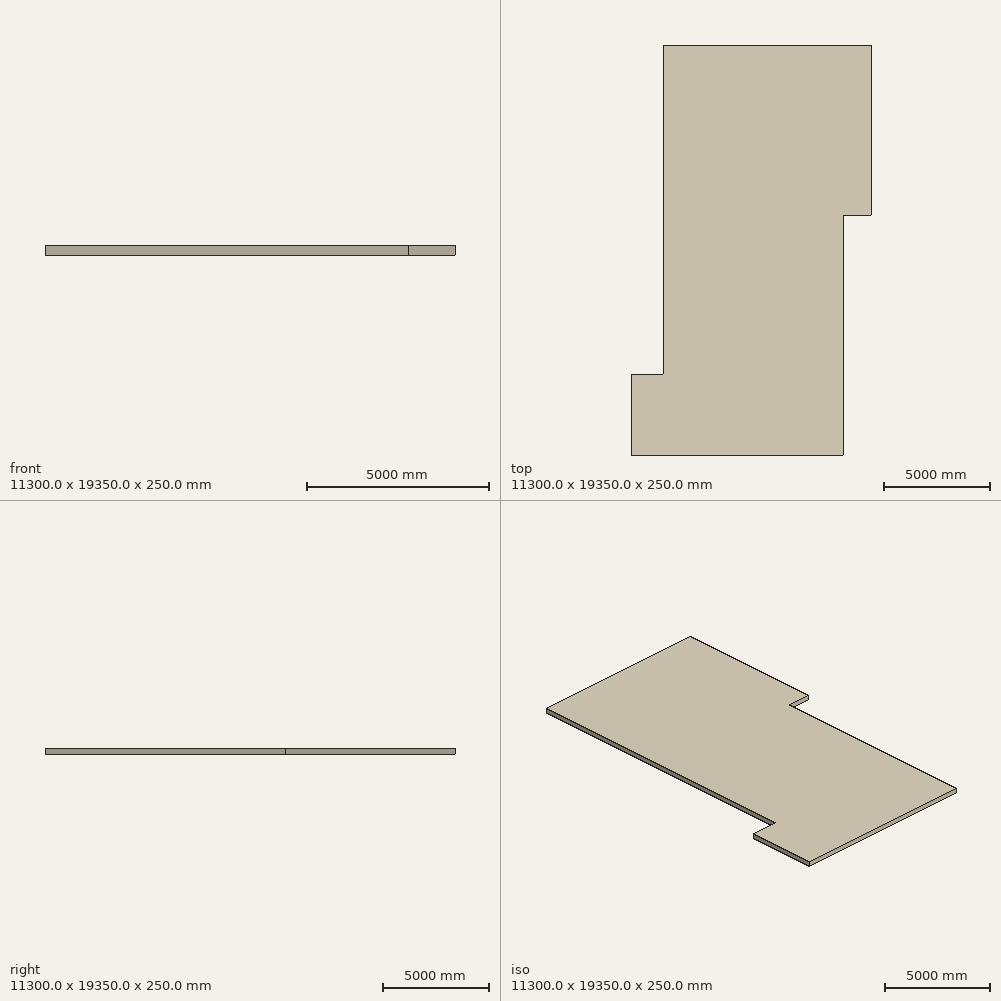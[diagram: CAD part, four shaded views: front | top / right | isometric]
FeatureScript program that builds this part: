
annotation { "Feature Type Name" : "Feature", "Feature Type Description" : "" }
export const myFeature = defineFeature(function(context is Context, id is Id, definition is map)
    precondition{}
    {
        {
            var Q0;
            Q0=qCreatedBy(makeId("Top.planeOp"),FACE);
            var sketch = newSketch(context, id + "F0", { "sketchPlane" : qUnion([Q0])});
            skLineSegment(sketch, "E0.bottom", {"start": v(-8628.68, 11353.51) * mm, "end": v(621.32, 11353.51) * mm});
            skLineSegment(sketch, "E0.top", {"start": v(-6878.68, 3353.51) * mm, "end": v(621.32, 3353.51) * mm});
            skLineSegment(sketch, "E0.right", {"start": v(621.32, 11353.51) * mm, "end": v(621.32, 3353.51) * mm});
            skLineSegment(sketch, "E1", {"start": v(-6878.68, 3353.51) * mm, "end": v(-8628.68, 11353.51) * mm});
            skSolve(sketch);
        }
        {
            var Q0;
            Q0 = qSketchRegion(id + "F0", true);
            extrude(context, id + "F1", {"entities" : qUnion([Q0]), "oppositeDirection" : true, "depth" : 250 * mm});
        }
        {
            var Q0;
            Q0=makeQuery(id+"F1.opExtrude","CAP_FACE",FACE,{"disambiguationData":[OSD([sQuery(id+"F0.wireOp",EDGE,"E0.bottom"),sQuery(id+"F0.wireOp",EDGE,"E0.top"),sQuery(id+"F0.wireOp",EDGE,"E0.right"),sQuery(id+"F0.wireOp",EDGE,"E1")])],"isStart":true});
            var sketch = newSketch(context, id + "F2", { "sketchPlane" : qUnion([Q0])});
            skLineSegment(sketch, "E2.bottom", {"start": v(-678.68, 3353.51) * mm, "end": v(-10678.68, 3353.51) * mm});
            skLineSegment(sketch, "E2.top", {"start": v(-678.68, -7996.49) * mm, "end": v(-10678.68, -7996.49) * mm});
            skLineSegment(sketch, "E2.left", {"start": v(-678.68, 3353.51) * mm, "end": v(-678.68, -7996.49) * mm});
            skLineSegment(sketch, "E2.right", {"start": v(-10678.68, 3353.51) * mm, "end": v(-10678.68, -7996.49) * mm});
            skSolve(sketch);
        }
        {
            var Q0;
            Q0 = qSketchRegion(id + "F2", true);
            extrude(context, id + "F3", {"entities" : qUnion([Q0]), "operationType" : NewBodyOperationType.ADD, "oppositeDirection" : true, "depth" : 250 * mm});
        }
        {
            var Q0;
            Q0=makeQuery(id+"F3.boolean.opBoolean","MERGE",FACE,{"derivedFrom":[makeQuery(id+"F1.opExtrude","CAP_FACE",FACE,{"disambiguationData":[OSD([sQuery(id+"F0.wireOp",EDGE,"E0.bottom"),sQuery(id+"F0.wireOp",EDGE,"E0.top"),sQuery(id+"F0.wireOp",EDGE,"E0.right"),sQuery(id+"F0.wireOp",EDGE,"E1")])],"isStart":true}),makeQuery(id+"F3.opExtrude","CAP_FACE",FACE,{"disambiguationData":[OSD([sQuery(id+"F2.wireOp",EDGE,"E2.bottom"),sQuery(id+"F2.wireOp",EDGE,"E2.top"),sQuery(id+"F2.wireOp",EDGE,"E2.left"),sQuery(id+"F2.wireOp",EDGE,"E2.right")])],"isStart":true})]});
            var sketch = newSketch(context, id + "F4", { "sketchPlane" : qUnion([Q0])});
            skLineSegment(sketch, "E3", {"start": v(-10678.68, -4196.49) * mm, "end": v(-5227.12, -4196.49) * mm});
            skLineSegment(sketch, "E4", {"start": v(-5227.12, -4196.49) * mm, "end": v(-6878.68, 3353.51) * mm});
            skSolve(sketch);
        }
        {
            var Q0;
            Q0 = qSketchRegion(id + "F4", true);
            var Q1;
            {var subQ0=sQuery(id+"F4.wireOp",EDGE,"E3");Q1=makeQuery(id+"F4.imprint","IMPRINT",FACE,{"disambiguationData":[TD([[makeQuery(id+"F4.imprint","IMPRINT",EDGE,{"derivedFrom":subQ0}),1.0]])]});}
            extrude(context, id + "F5", {"entities" : qUnion([Q0, Q1]), "operationType" : NewBodyOperationType.REMOVE, "endBound" : BoundingType.UP_TO_NEXT, "oppositeDirection" : true, "depth" : 25 * mm});
        }
        {
            var Q0;
            Q0=makeQuery(id+"F3.boolean.opBoolean","MERGE",FACE,{"derivedFrom":[makeQuery(id+"F1.opExtrude","CAP_FACE",FACE,{"disambiguationData":[OSD([sQuery(id+"F0.wireOp",EDGE,"E0.bottom"),sQuery(id+"F0.wireOp",EDGE,"E0.top"),sQuery(id+"F0.wireOp",EDGE,"E0.right"),sQuery(id+"F0.wireOp",EDGE,"E1")])],"isStart":true}),makeQuery(id+"F3.opExtrude","CAP_FACE",FACE,{"disambiguationData":[OSD([sQuery(id+"F2.wireOp",EDGE,"E2.bottom"),sQuery(id+"F2.wireOp",EDGE,"E2.top"),sQuery(id+"F2.wireOp",EDGE,"E2.left"),sQuery(id+"F2.wireOp",EDGE,"E2.right")])],"isStart":true})]});
            var sketch = newSketch(context, id + "F6", { "sketchPlane" : qUnion([Q0])});
            skLineSegment(sketch, "E5", {"start": v(-9178.68, 11353.51) * mm, "end": v(-9178.68, -4196.49) * mm});
            skLineSegment(sketch, "E6", {"start": v(-8628.68, 11353.51) * mm, "end": v(-9178.68, 11353.51) * mm});
            skSolve(sketch);
        }
        {
            var Q0;
            Q0 = qSketchRegion(id + "F6", true);
            var Q1;
            {var subQ0=sQuery(id+"F6.wireOp",EDGE,"E5");Q1=makeQuery(id+"F6.imprint","IMPRINT",FACE,{"disambiguationData":[TD([[makeQuery(id+"F6.imprint","IMPRINT",EDGE,{"derivedFrom":subQ0}),1.0]])]});}
            extrude(context, id + "F7", {"entities" : qUnion([Q0, Q1]), "operationType" : NewBodyOperationType.ADD, "oppositeDirection" : true, "depth" : 250 * mm});
        }
    });
